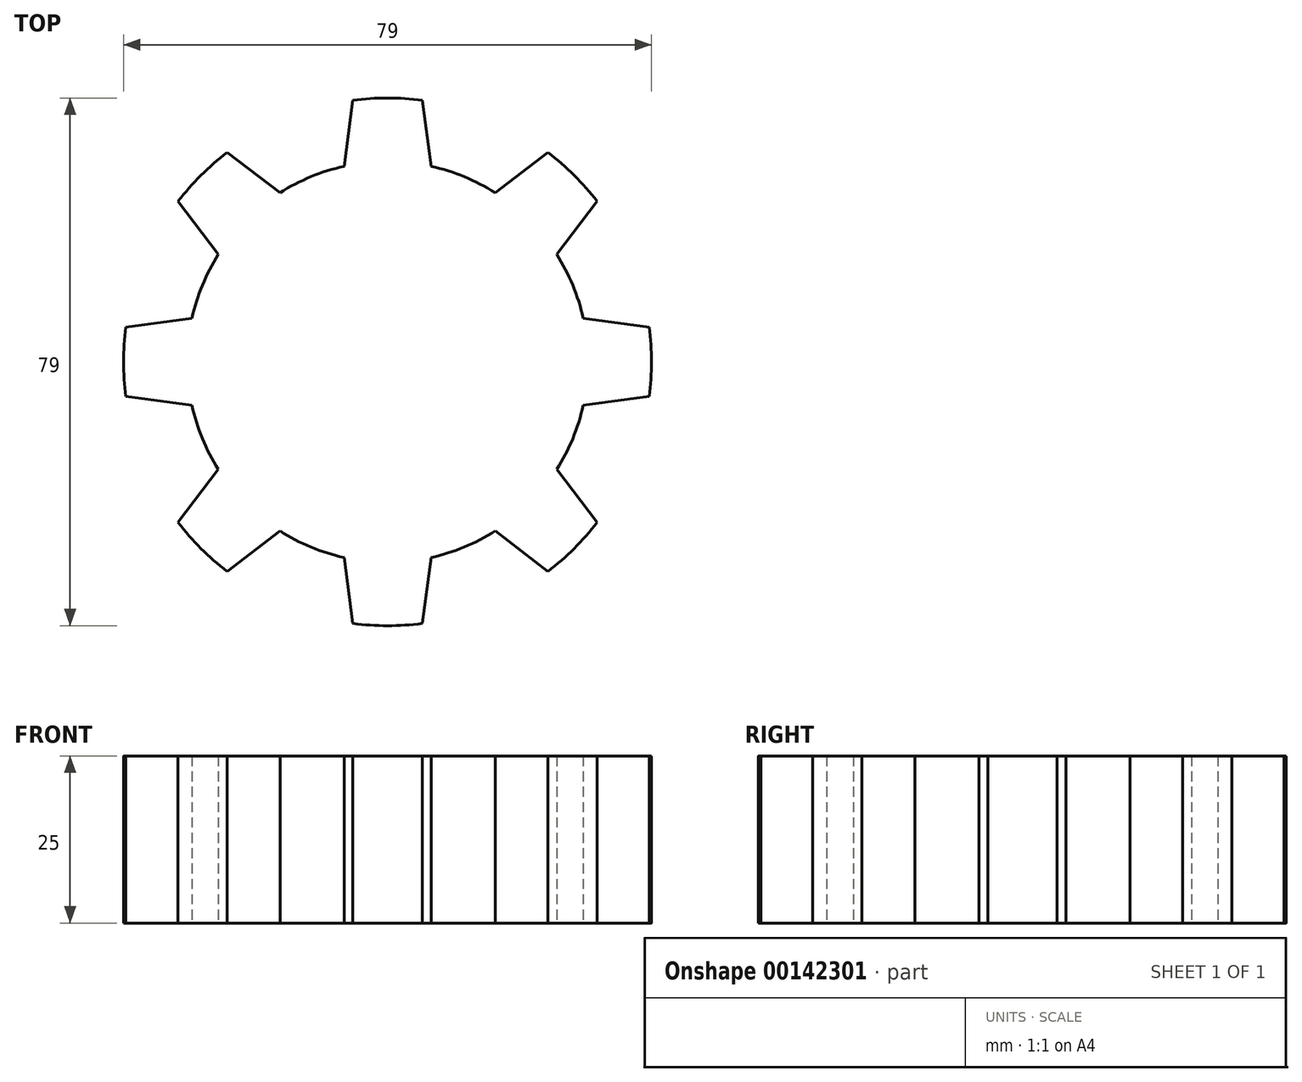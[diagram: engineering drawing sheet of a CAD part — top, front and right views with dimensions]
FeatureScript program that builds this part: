
annotation { "Feature Type Name" : "Feature", "Feature Type Description" : "" }
export const myFeature = defineFeature(function(context is Context, id is Id, definition is map)
    precondition{}
    {
        {
            var Q0;
            Q0=qCreatedBy(makeId("Top.planeOp"),FACE);
            var sketch = newSketch(context, id + "F0", { "sketchPlane" : qUnion([Q0])});
            skCircle(sketch, "E0", {"center": v(35, 0) * mm, "radius": 30 * mm, "construction": true});
            skCircle(sketch, "E1", {"center": v(35, 0) * mm, "radius": 39.5 * mm, "construction": true});
            skCircle(sketch, "E2", {"center": v(-35, 0) * mm, "radius": 30 * mm, "construction": true});
            skCircle(sketch, "E3", {"center": v(-35, 0) * mm, "radius": 39.5 * mm, "construction": true});
            skLineSegment(sketch, "E4", {"start": v(-35, 0) * mm, "end": v(35, 0) * mm, "construction": true});
            skLineSegment(sketch, "E5", {"start": v(35, 0) * mm, "end": v(35, -54.86) * mm, "construction": true});
            skLineSegment(sketch, "E6", {"start": v(40.19, -39.16) * mm, "end": v(41.52, -29.28) * mm});
            skLineSegment(sketch, "E7", {"start": v(29.81, -39.16) * mm, "end": v(28.48, -29.28) * mm});
            skArc(sketch, "E8", {"start": v(29.81, -39.16) * mm, "mid": v(35, -39.5) * mm, "end": v(40.19, -39.16) * mm});
            skArc(sketch, "E9", {"start": v(18.9, -25.31) * mm, "mid": v(23.52, -27.72) * mm, "end": v(28.48, -29.28) * mm});
            skLineSegment(sketch, "E10", {"start": v(29.81, -39.16) * mm, "end": v(40.19, -39.16) * mm, "construction": true});
            skLineSegment(sketch, "E11", {"start": v(28.48, -29.28) * mm, "end": v(18.9, -25.31) * mm, "construction": true});
            skLineSegment(sketch, "E12", {"start": v(29.81, -39.16) * mm, "end": v(35, 0) * mm, "construction": true});
            skLineSegment(sketch, "E13", {"start": v(40.19, -39.16) * mm, "end": v(35, 0) * mm, "construction": true});
            skLineSegment(sketch, "E14", {"start": v(18.9, -25.31) * mm, "end": v(35, 0) * mm, "construction": true});
            skLineSegment(sketch, "E15", {"start": v(28.48, -29.28) * mm, "end": v(35, 0) * mm, "construction": true});
            skArc(sketch, "E16.1.0", {"start": v(41.52, -29.28) * mm, "mid": v(46.48, -27.72) * mm, "end": v(51.1, -25.31) * mm});
            skLineSegment(sketch, "E16.1.1", {"start": v(59.02, -31.36) * mm, "end": v(51.1, -25.31) * mm});
            skLineSegment(sketch, "E16.1.2", {"start": v(66.36, -24.02) * mm, "end": v(60.31, -16.1) * mm});
            skArc(sketch, "E16.1.3", {"start": v(59.02, -31.36) * mm, "mid": v(62.93, -27.93) * mm, "end": v(66.36, -24.02) * mm});
            skArc(sketch, "E16.2.0", {"start": v(60.31, -16.1) * mm, "mid": v(62.72, -11.48) * mm, "end": v(64.28, -6.52) * mm});
            skLineSegment(sketch, "E16.2.1", {"start": v(74.16, -5.19) * mm, "end": v(64.28, -6.52) * mm});
            skLineSegment(sketch, "E16.2.2", {"start": v(74.16, 5.19) * mm, "end": v(64.28, 6.52) * mm});
            skArc(sketch, "E16.2.3", {"start": v(74.16, -5.19) * mm, "mid": v(74.5, 0) * mm, "end": v(74.16, 5.19) * mm});
            skLineSegment(sketch, "E17.4.3.0", {"start": v(66.36, 24.02) * mm, "end": v(60.31, 16.1) * mm});
            skArc(sketch, "E17.5.3.0", {"start": v(64.28, 6.52) * mm, "mid": v(62.72, 11.48) * mm, "end": v(60.31, 16.1) * mm});
            skLineSegment(sketch, "E17.7.3.0", {"start": v(59.02, 31.36) * mm, "end": v(51.1, 25.31) * mm});
            skArc(sketch, "E17.10.3.0", {"start": v(66.36, 24.02) * mm, "mid": v(62.93, 27.93) * mm, "end": v(59.02, 31.36) * mm});
            skLineSegment(sketch, "E17.4.4.0", {"start": v(40.19, 39.16) * mm, "end": v(41.52, 29.28) * mm});
            skArc(sketch, "E17.5.4.0", {"start": v(51.1, 25.31) * mm, "mid": v(46.48, 27.72) * mm, "end": v(41.52, 29.28) * mm});
            skLineSegment(sketch, "E17.7.4.0", {"start": v(29.81, 39.16) * mm, "end": v(28.48, 29.28) * mm});
            skArc(sketch, "E17.10.4.0", {"start": v(40.19, 39.16) * mm, "mid": v(35, 39.5) * mm, "end": v(29.81, 39.16) * mm});
            skLineSegment(sketch, "E17.4.5.0", {"start": v(10.98, 31.36) * mm, "end": v(18.9, 25.31) * mm});
            skArc(sketch, "E17.5.5.0", {"start": v(28.48, 29.28) * mm, "mid": v(23.52, 27.72) * mm, "end": v(18.9, 25.31) * mm});
            skLineSegment(sketch, "E17.7.5.0", {"start": v(3.64, 24.02) * mm, "end": v(9.69, 16.1) * mm});
            skArc(sketch, "E17.10.5.0", {"start": v(10.98, 31.36) * mm, "mid": v(7.07, 27.93) * mm, "end": v(3.64, 24.02) * mm});
            skLineSegment(sketch, "E17.4.6.0", {"start": v(-4.16, 5.19) * mm, "end": v(5.72, 6.52) * mm});
            skArc(sketch, "E17.5.6.0", {"start": v(9.69, 16.1) * mm, "mid": v(7.28, 11.48) * mm, "end": v(5.72, 6.52) * mm});
            skLineSegment(sketch, "E17.7.6.0", {"start": v(-4.16, -5.19) * mm, "end": v(5.72, -6.52) * mm});
            skArc(sketch, "E17.10.6.0", {"start": v(-4.16, 5.19) * mm, "mid": v(-4.5, 0) * mm, "end": v(-4.16, -5.19) * mm});
            skLineSegment(sketch, "E17.4.7.0", {"start": v(3.64, -24.02) * mm, "end": v(9.69, -16.1) * mm});
            skArc(sketch, "E17.5.7.0", {"start": v(5.72, -6.52) * mm, "mid": v(7.28, -11.48) * mm, "end": v(9.69, -16.1) * mm});
            skLineSegment(sketch, "E17.7.7.0", {"start": v(10.98, -31.36) * mm, "end": v(18.9, -25.31) * mm});
            skArc(sketch, "E17.10.7.0", {"start": v(3.64, -24.02) * mm, "mid": v(7.07, -27.93) * mm, "end": v(10.98, -31.36) * mm});
            skLineSegment(sketch, "E18", {"start": v(0, 0) * mm, "end": v(0, 42.54) * mm, "construction": true});
            skSolve(sketch);
        }
        {
            var Q0;
            Q0 = qSketchRegion(id + "F0", true);
            var Q1;
            Q1=sQuery(id+"F0.wireOp",EDGE,"E17.5.4.0");
            var Q2;
            Q2=sQuery(id+"F0.wireOp",EDGE,"E17.5.6.0");
            var Q3;
            Q3=sQuery(id+"F0.wireOp",EDGE,"E16.2.2");
            var Q4;
            Q4=sQuery(id+"F0.wireOp",EDGE,"E17.5.3.0");
            var Q5;
            Q5=sQuery(id+"F0.wireOp",EDGE,"E17.4.3.0");
            var Q6;
            Q6=sQuery(id+"F0.wireOp",EDGE,"E16.2.1");
            var Q7;
            Q7=sQuery(id+"F0.wireOp",EDGE,"E17.4.4.0");
            var Q8;
            Q8=sQuery(id+"F0.wireOp",EDGE,"E17.4.7.0");
            var Q9;
            Q9=sQuery(id+"F0.wireOp",EDGE,"E17.10.5.0");
            var Q10;
            Q10=sQuery(id+"F0.wireOp",EDGE,"E17.5.7.0");
            var Q11;
            Q11=sQuery(id+"F0.wireOp",EDGE,"E17.5.5.0");
            var Q12;
            Q12=sQuery(id+"F0.wireOp",EDGE,"E16.1.1");
            var Q13;
            Q13=sQuery(id+"F0.wireOp",EDGE,"E17.7.4.0");
            var Q14;
            Q14=sQuery(id+"F0.wireOp",EDGE,"E17.7.6.0");
            var Q15;
            Q15=sQuery(id+"F0.wireOp",EDGE,"E17.10.4.0");
            var Q16;
            Q16=sQuery(id+"F0.wireOp",EDGE,"E17.4.5.0");
            var Q17;
            Q17=sQuery(id+"F0.wireOp",EDGE,"E16.1.0");
            var Q18;
            Q18=sQuery(id+"F0.wireOp",EDGE,"E17.4.6.0");
            var Q19;
            Q19=sQuery(id+"F0.wireOp",EDGE,"E16.2.0");
            var Q20;
            Q20=sQuery(id+"F0.wireOp",EDGE,"E17.10.6.0");
            var Q21;
            Q21=sQuery(id+"F0.wireOp",EDGE,"E16.2.3");
            var Q22;
            Q22=sQuery(id+"F0.wireOp",EDGE,"E17.10.3.0");
            var Q23;
            Q23=sQuery(id+"F0.wireOp",EDGE,"E17.10.7.0");
            var Q24;
            Q24=sQuery(id+"F0.wireOp",EDGE,"E9");
            var Q25;
            Q25=sQuery(id+"F0.wireOp",EDGE,"E8");
            var Q26;
            Q26=sQuery(id+"F0.wireOp",EDGE,"E7");
            var Q27;
            Q27=sQuery(id+"F0.wireOp",EDGE,"E6");
            var Q28;
            Q28=sQuery(id+"F0.wireOp",EDGE,"E16.1.3");
            var Q29;
            Q29=sQuery(id+"F0.wireOp",EDGE,"E16.1.2");
            var Q30;
            Q30=sQuery(id+"F0.wireOp",EDGE,"E17.7.7.0");
            var Q31;
            Q31=sQuery(id+"F0.wireOp",EDGE,"E17.7.3.0");
            var Q32;
            Q32=sQuery(id+"F0.wireOp",EDGE,"E17.7.5.0");
            extrude(context, id + "F1", {"entities" : qUnion([Q0]), "surfaceEntities" : qUnion([Q1, Q2, Q3, Q4, Q5, Q6, Q7, Q8, Q9, Q10, Q11, Q12, Q13, Q14, Q15, Q16, Q17, Q18, Q19, Q20, Q21, Q22, Q23, Q24, Q25, Q26, Q27, Q28, Q29, Q30, Q31, Q32]), "depth" : 25 * mm});
        }
    });
